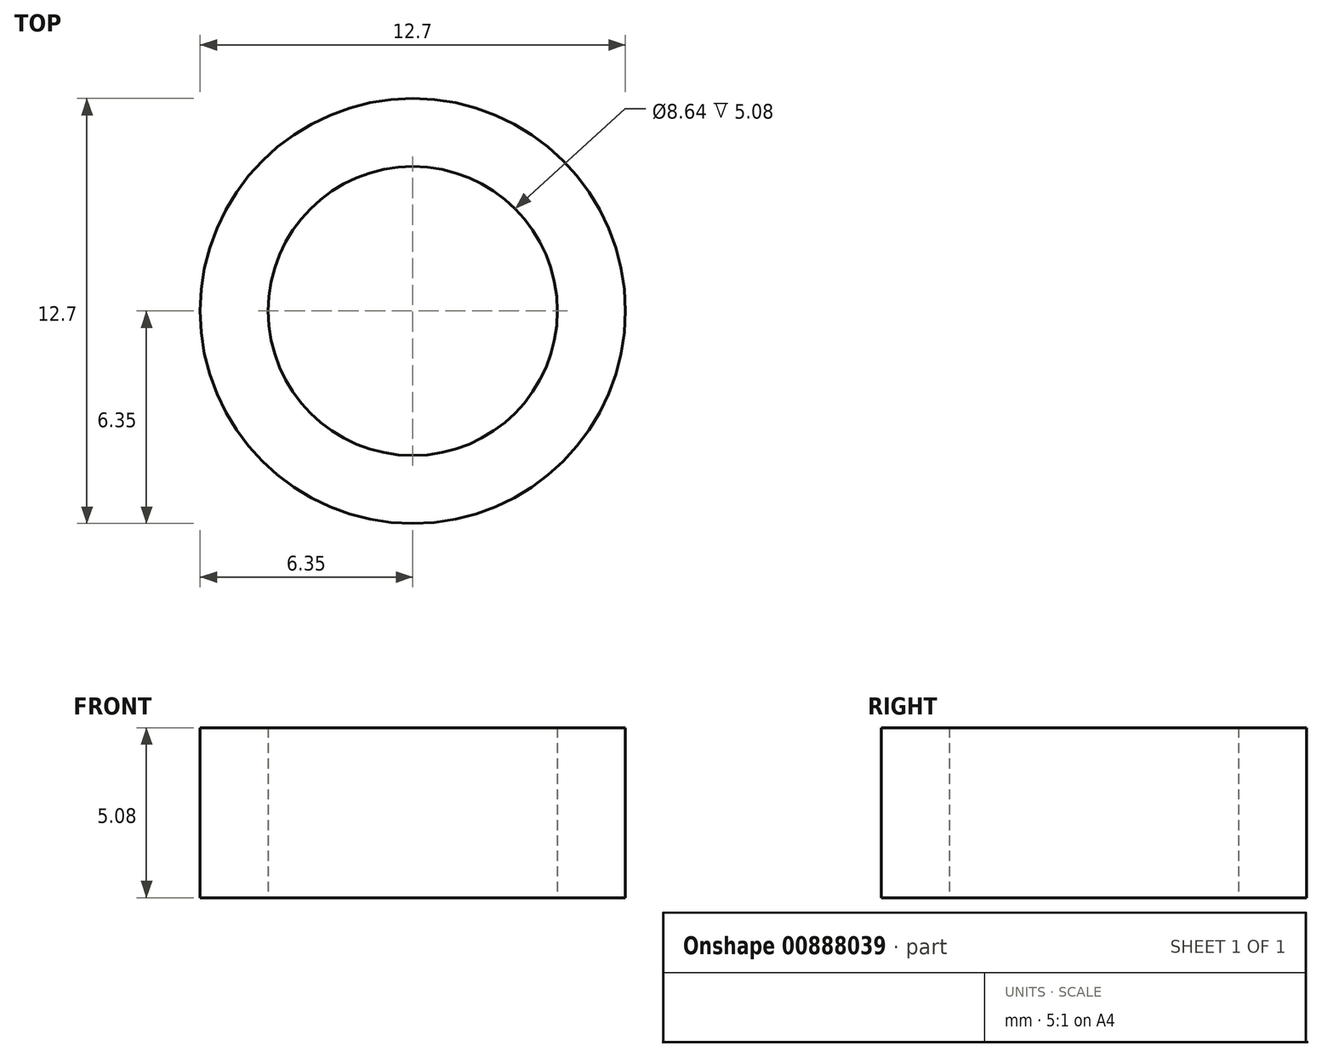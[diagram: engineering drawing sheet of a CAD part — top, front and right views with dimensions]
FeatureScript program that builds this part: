
annotation { "Feature Type Name" : "Feature", "Feature Type Description" : "" }
export const myFeature = defineFeature(function(context is Context, id is Id, definition is map)
    precondition{}
    {
        {
            var Q0;
            Q0=qCreatedBy(makeId("Top.planeOp"),FACE);
            var sketch = newSketch(context, id + "F0", { "sketchPlane" : qUnion([Q0])});
            skCircle(sketch, "E0", {"center": v(0, 0) * mm, "radius": 4.32 * mm});
            skCircle(sketch, "E1", {"center": v(0, 0) * mm, "radius": 6.35 * mm});
            skSolve(sketch);
        }
        {
            var Q0;
            Q0=makeQuery(id+"F0.imprint","IMPRINT",FACE,{"disambiguationData":[TD([[makeQuery(id+"F0.imprint","IMPRINT",EDGE,{"derivedFrom":sQuery(id+"F0.wireOp",EDGE,"E0")}),-1.0]])]});
            extrude(context, id + "F1", {"entities" : qUnion([Q0]), "depth" : 5.08 * mm, "offsetDistance" : 25.4 * mm});
        }
    });
